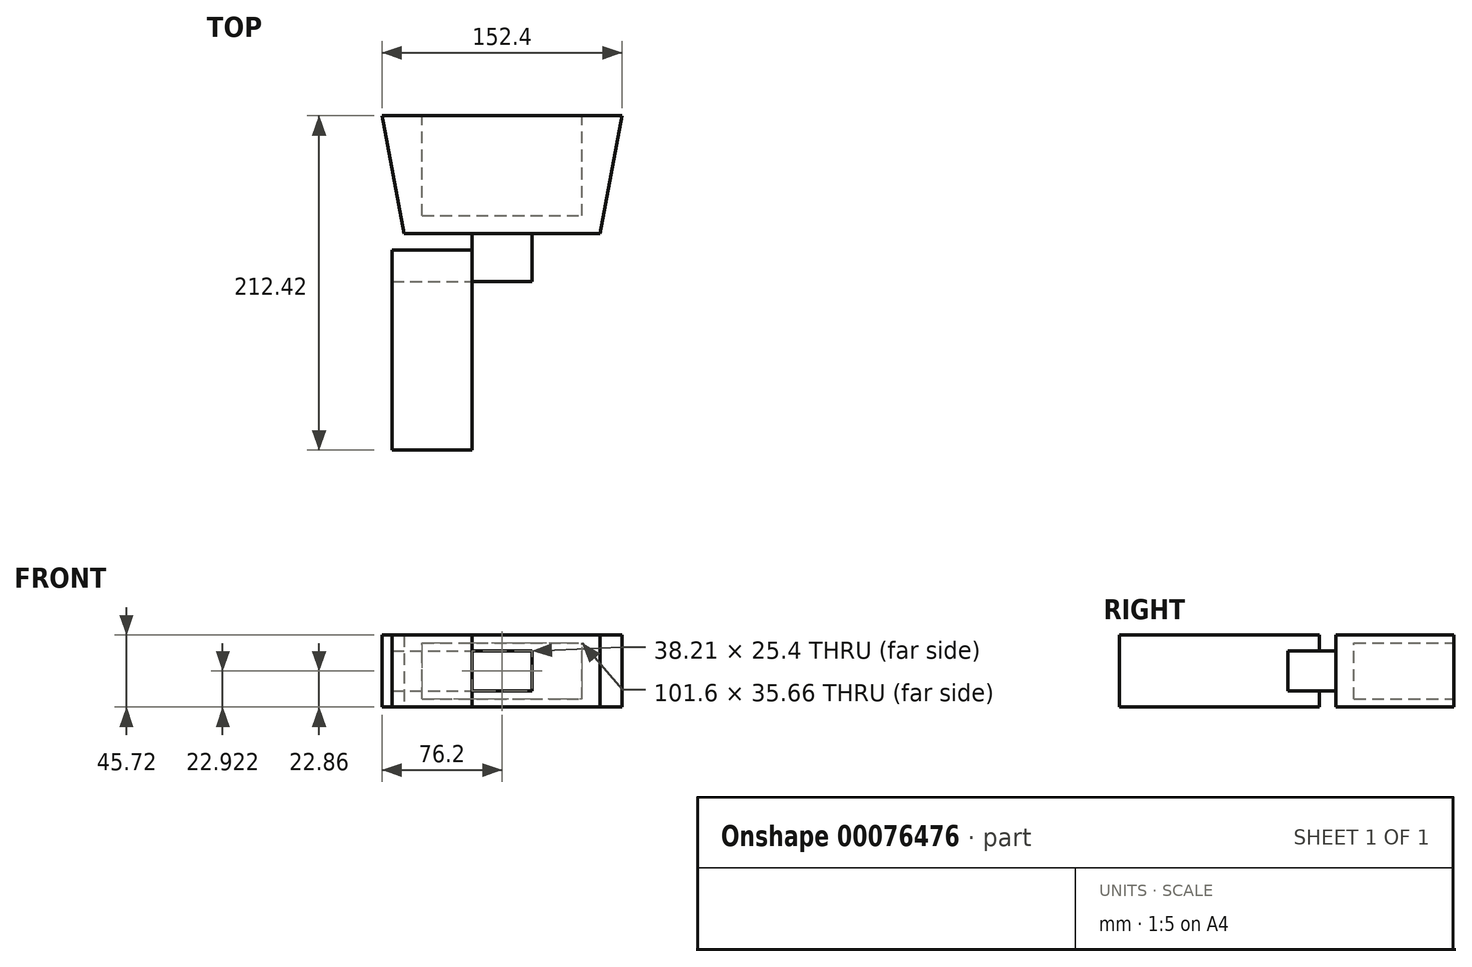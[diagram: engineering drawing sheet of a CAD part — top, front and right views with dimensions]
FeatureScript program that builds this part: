
annotation { "Feature Type Name" : "Feature", "Feature Type Description" : "" }
export const myFeature = defineFeature(function(context is Context, id is Id, definition is map)
    precondition{}
    {
        {
            var Q0;
            Q0=qCreatedBy(makeId("Top.planeOp"),FACE);
            var sketch = newSketch(context, id + "F0", { "sketchPlane" : qUnion([Q0])});
            skLineSegment(sketch, "E0", {"start": v(0, 109.3) * mm, "end": v(-25.4, 109.3) * mm});
            skLineSegment(sketch, "E1", {"start": v(0, 109.3) * mm, "end": v(25.4, 109.3) * mm});
            skLineSegment(sketch, "E2", {"start": v(-25.4, 109.3) * mm, "end": v(-25.4, 87.08) * mm});
            skLineSegment(sketch, "E3", {"start": v(25.4, 109.3) * mm, "end": v(25.4, 87.08) * mm});
            skLineSegment(sketch, "E4", {"start": v(-25.4, 87.08) * mm, "end": v(-50.8, 87.08) * mm});
            skLineSegment(sketch, "E5", {"start": v(25.4, 87.08) * mm, "end": v(50.8, 87.08) * mm});
            skLineSegment(sketch, "E6", {"start": v(-50.8, 87.08) * mm, "end": v(-50.8, -119.3) * mm});
            skLineSegment(sketch, "E7", {"start": v(50.8, 87.08) * mm, "end": v(50.8, -119.3) * mm});
            skLineSegment(sketch, "E8", {"start": v(-25.4, 74.38) * mm, "end": v(25.4, 74.38) * mm});
            skLineSegment(sketch, "E9", {"start": v(-25.4, 74.38) * mm, "end": v(-25.4, 1.78) * mm});
            skLineSegment(sketch, "E10", {"start": v(-25.4, 1.78) * mm, "end": v(25.4, 1.78) * mm});
            skLineSegment(sketch, "E11", {"start": v(25.4, 1.78) * mm, "end": v(25.4, 74.38) * mm});
            skLineSegment(sketch, "E12", {"start": v(-50.8, -119.3) * mm, "end": v(-76.2, -119.3) * mm});
            skLineSegment(sketch, "E13", {"start": v(-76.2, -119.3) * mm, "end": v(-62.28, -194.22) * mm});
            skLineSegment(sketch, "E14", {"start": v(0, 74.38) * mm, "end": v(0, -119.3) * mm});
            skLineSegment(sketch, "E15.MirrorCS", {"start": v(50.8, -119.3) * mm, "end": v(76.2, -119.3) * mm});
            skLineSegment(sketch, "E16.MirrorCS", {"start": v(76.2, -119.3) * mm, "end": v(62.28, -194.22) * mm});
            skLineSegment(sketch, "E17", {"start": v(-62.28, -194.22) * mm, "end": v(62.28, -194.22) * mm});
            skLineSegment(sketch, "E18", {"start": v(-50.8, -119.3) * mm, "end": v(50.8, -119.3) * mm});
            skSolve(sketch);
        }
        {
            var Q0;
            {var subQ0=sQuery(id+"F0.wireOp",EDGE,"E12");Q0=makeQuery(id+"F0.imprint","IMPRINT",FACE,{"disambiguationData":[TD([[makeQuery(id+"F0.imprint","IMPRINT",EDGE,{"derivedFrom":subQ0}),1.0]])]});}
            extrude(context, id + "F1", {"entities" : qUnion([Q0]), "depth" : 45.72 * mm});
        }
        {
            var Q0;
            Q0=makeQuery(id+"F1.opExtrude","SWEPT_FACE",FACE,{"disambiguationData":[OSD([sQuery(id+"F0.wireOp",EDGE,"E12"),sQuery(id+"F0.wireOp",EDGE,"E15.MirrorCS"),sQuery(id+"F0.wireOp",EDGE,"E18")])]});
            var sketch = newSketch(context, id + "F2", { "sketchPlane" : qUnion([Q0])});
            skLineSegment(sketch, "E19", {"start": v(50.8, 5.1) * mm, "end": v(50.8, 40.75) * mm});
            skLineSegment(sketch, "E20", {"start": v(-50.8, 5.1) * mm, "end": v(-50.8, 40.75) * mm});
            skLineSegment(sketch, "E21.bottom", {"start": v(-76.2, 45.72) * mm, "end": v(-76.2, 45.72) * mm});
            skLineSegment(sketch, "E21.top", {"start": v(-76.2, 0) * mm, "end": v(-76.2, 0) * mm});
            skLineSegment(sketch, "E21.left", {"start": v(-76.2, 45.72) * mm, "end": v(-76.2, 0) * mm});
            skLineSegment(sketch, "E21.right", {"start": v(-76.2, 45.72) * mm, "end": v(-76.2, 0) * mm});
            skLineSegment(sketch, "E22", {"start": v(-50.8, 40.75) * mm, "end": v(-50.8, 43.24) * mm});
            skLineSegment(sketch, "E23", {"start": v(-50.8, 43.24) * mm, "end": v(50.8, 43.24) * mm});
            skLineSegment(sketch, "E24", {"start": v(50.8, 43.24) * mm, "end": v(50.8, 40.75) * mm});
            skLineSegment(sketch, "E25", {"start": v(-50.8, 5.1) * mm, "end": v(-50.8, 2.6) * mm});
            skLineSegment(sketch, "E26", {"start": v(-50.8, 2.6) * mm, "end": v(50.8, 2.6) * mm});
            skLineSegment(sketch, "E27", {"start": v(50.8, 2.6) * mm, "end": v(50.8, 5.1) * mm});
            skLineSegment(sketch, "E28", {"start": v(-50.8, 40.75) * mm, "end": v(50.8, 40.75) * mm});
            skLineSegment(sketch, "E29", {"start": v(-50.8, 5.1) * mm, "end": v(50.8, 5.1) * mm});
            skSolve(sketch);
        }
        {
            var Q0;
            Q0=makeQuery(id+"F2.imprint","IMPRINT",FACE,{"disambiguationData":[TD([[makeQuery(id+"F2.imprint","IMPRINT",EDGE,{"derivedFrom":sQuery(id+"F2.wireOp",EDGE,"E19")}),1.0]])]});
            extrude(context, id + "F3", {"entities" : qUnion([Q0]), "operationType" : NewBodyOperationType.REMOVE, "oppositeDirection" : true, "depth" : 63.5 * mm});
        }
        {
            var Q0;
            Q0=makeQuery(id+"F1.opExtrude","SWEPT_FACE",FACE,{"disambiguationData":[OSD([sQuery(id+"F0.wireOp",EDGE,"E17")])]});
            var sketch = newSketch(context, id + "F4", { "sketchPlane" : qUnion([Q0])});
            skLineSegment(sketch, "E30", {"start": v(-62.28, 45.72) * mm, "end": v(62.28, 45.72) * mm});
            skLineSegment(sketch, "E31", {"start": v(-62.28, 45.72) * mm, "end": v(-62.28, 35.56) * mm});
            skLineSegment(sketch, "E32", {"start": v(-62.28, 35.56) * mm, "end": v(-62.28, 10.16) * mm});
            skLineSegment(sketch, "E33", {"start": v(-62.28, 10.16) * mm, "end": v(-62.28, 0) * mm});
            skLineSegment(sketch, "E34", {"start": v(62.28, 45.72) * mm, "end": v(62.28, 35.56) * mm});
            skLineSegment(sketch, "E35", {"start": v(62.28, 35.56) * mm, "end": v(62.28, 10.16) * mm});
            skLineSegment(sketch, "E36", {"start": v(62.28, 10.16) * mm, "end": v(62.28, 0) * mm});
            skLineSegment(sketch, "E37", {"start": v(-19.1, 45.72) * mm, "end": v(19.1, 45.72) * mm});
            skLineSegment(sketch, "E38", {"start": v(-62.28, 0) * mm, "end": v(-19.1, 0) * mm});
            skLineSegment(sketch, "E39", {"start": v(-19.1, 0) * mm, "end": v(12.47, 0) * mm});
            skLineSegment(sketch, "E40", {"start": v(12.47, 0) * mm, "end": v(62.28, 0) * mm});
            skLineSegment(sketch, "E41", {"start": v(-19.1, 35.56) * mm, "end": v(19.1, 35.56) * mm});
            skLineSegment(sketch, "E42", {"start": v(19.1, 35.56) * mm, "end": v(19.1, 10.16) * mm});
            skLineSegment(sketch, "E43", {"start": v(19.1, 10.16) * mm, "end": v(-19.1, 10.16) * mm});
            skLineSegment(sketch, "E44", {"start": v(-19.1, 10.16) * mm, "end": v(-19.1, 35.56) * mm});
            skSolve(sketch);
        }
        {
            var Q0;
            Q0=makeQuery(id+"F4.imprint","IMPRINT",FACE,{"disambiguationData":[TD([[makeQuery(id+"F4.imprint","IMPRINT",EDGE,{"derivedFrom":sQuery(id+"F4.wireOp",EDGE,"E41")}),-1.0]])]});
            extrude(context, id + "F5", {"entities" : qUnion([Q0]), "operationType" : NewBodyOperationType.ADD, "depth" : 30.48 * mm});
        }
        {
            var Q0;
            Q0=makeQuery(id+"F5.opExtrude","SWEPT_FACE",FACE,{"disambiguationData":[OSD([sQuery(id+"F4.wireOp",EDGE,"E44")])]});
            var sketch = newSketch(context, id + "F6", { "sketchPlane" : qUnion([Q0])});
            skLineSegment(sketch, "E45.bottom", {"start": v(204.72, 0) * mm, "end": v(331.72, 0) * mm});
            skLineSegment(sketch, "E45.top", {"start": v(204.72, 45.72) * mm, "end": v(331.72, 45.72) * mm});
            skLineSegment(sketch, "E45.left", {"start": v(204.72, 0) * mm, "end": v(204.72, 45.72) * mm});
            skLineSegment(sketch, "E45.right", {"start": v(331.72, 0) * mm, "end": v(331.72, 45.72) * mm});
            skLineSegment(sketch, "E46", {"start": v(204.72, 10.16) * mm, "end": v(204.72, 35.56) * mm});
            skSolve(sketch);
        }
        {
            var Q0;
            {var subQ0=sQuery(id+"F6.wireOp",EDGE,"E46");Q0=makeQuery(id+"F6.imprint","IMPRINT",FACE,{"disambiguationData":[TD([[makeQuery(id+"F6.imprint","IMPRINT",EDGE,{"derivedFrom":subQ0}),-1.0]])]});}
            var Q1;
            {var subQ6=sQuery(id+"F6.wireOp",EDGE,"E45.bottom");Q1=makeQuery(id+"F6.imprint","IMPRINT",FACE,{"disambiguationData":[TD([[makeQuery(id+"F6.imprint","IMPRINT",EDGE,{"derivedFrom":subQ6}),1.0]])]});}
            extrude(context, id + "F7", {"entities" : qUnion([Q0, Q1]), "operationType" : NewBodyOperationType.ADD, "depth" : 50.8 * mm});
        }
        {
            var Q0;
            Q0=makeQuery(id+"F1.opExtrude","SWEPT_BODY",BODY,{"disambiguationData":[OSD([sQuery(id+"F0.wireOp",EDGE,"E12"),sQuery(id+"F0.wireOp",EDGE,"E13"),sQuery(id+"F0.wireOp",EDGE,"E15.MirrorCS"),sQuery(id+"F0.wireOp",EDGE,"E16.MirrorCS"),sQuery(id+"F0.wireOp",EDGE,"E17"),sQuery(id+"F0.wireOp",EDGE,"E18")])]});
            var Q1;
            Q1=qCreatedBy(makeId("Right.planeOp"),FACE);
            mirror(context, id + "F8", {"operationType" : NewBodyOperationType.ADD, "entities" : qUnion([Q0]), "mirrorPlane" : qUnion([Q1])});
        }
    });
